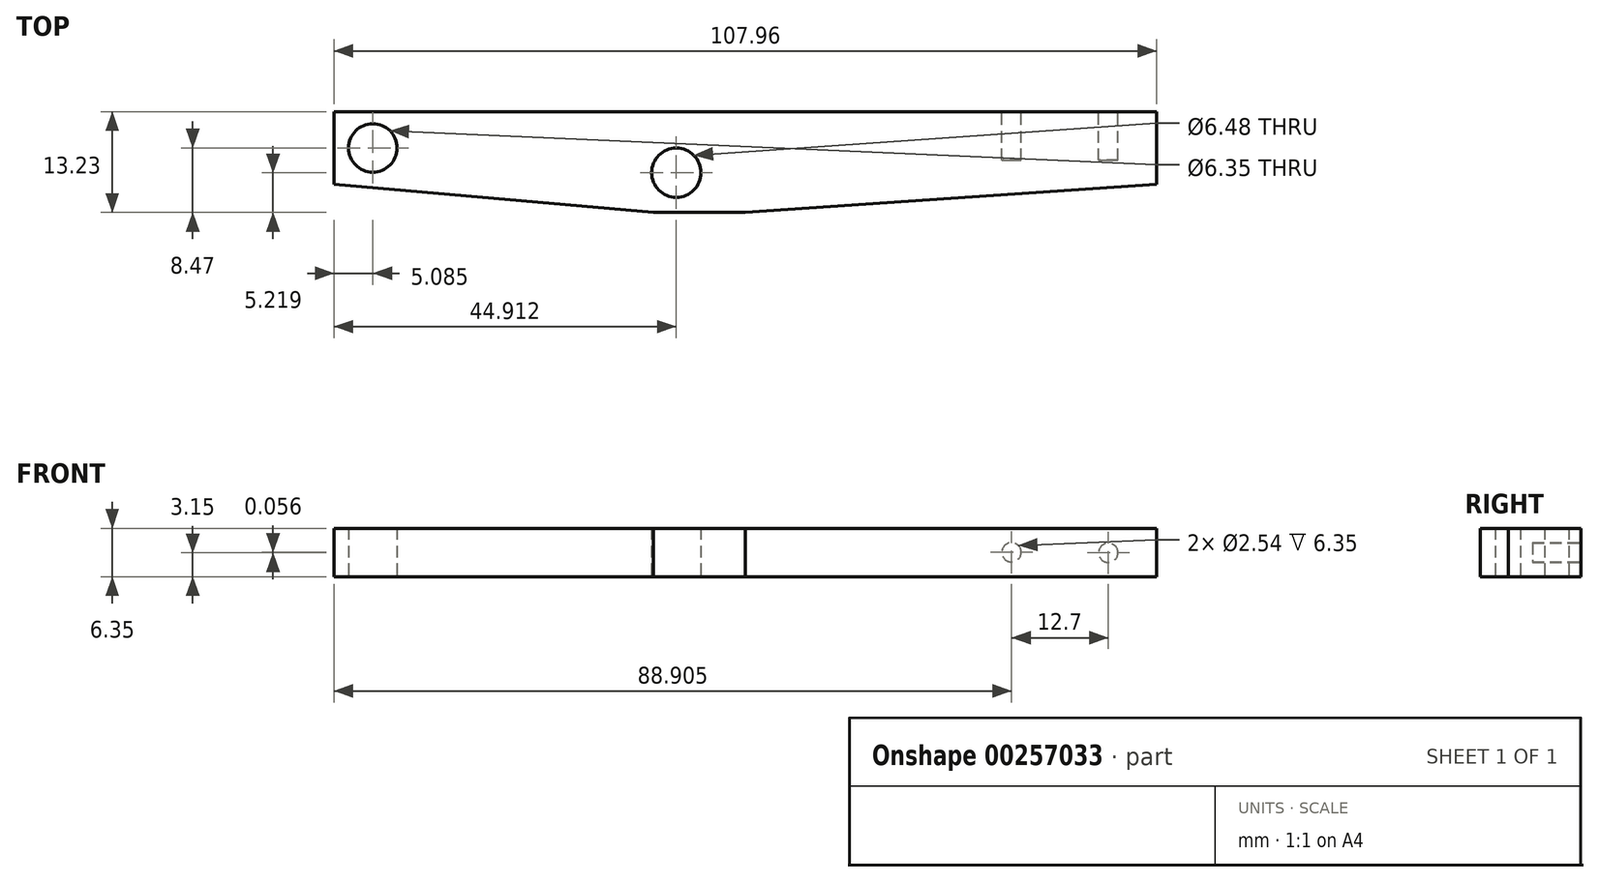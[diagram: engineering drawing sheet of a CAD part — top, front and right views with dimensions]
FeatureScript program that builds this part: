
annotation { "Feature Type Name" : "Feature", "Feature Type Description" : "" }
export const myFeature = defineFeature(function(context is Context, id is Id, definition is map)
    precondition{}
    {
        {
            var Q0;
            Q0=qCreatedBy(makeId("Top.planeOp"),FACE);
            var sketch = newSketch(context, id + "F0", { "sketchPlane" : qUnion([Q0])});
            skLineSegment(sketch, "E0.bottom", {"start": v(53.98, 4.76) * mm, "end": v(-53.98, 4.76) * mm});
            skLineSegment(sketch, "E0.top", {"start": v(53.98, -4.76) * mm, "end": v(-53.98, -4.76) * mm});
            skLineSegment(sketch, "E0.left", {"start": v(53.98, 4.76) * mm, "end": v(53.98, -4.76) * mm});
            skLineSegment(sketch, "E0.right", {"start": v(-53.98, 4.76) * mm, "end": v(-53.98, -4.76) * mm});
            skPoint(sketch, "E0.middle", {"position": v(0, 0) * mm});
            skLineSegment(sketch, "E1", {"start": v(-53.98, -4.76) * mm, "end": v(-12.07, -8.47) * mm});
            skLineSegment(sketch, "E2", {"start": v(-12.06, -8.47) * mm, "end": v(0, -8.47) * mm});
            skLineSegment(sketch, "E3", {"start": v(0, -8.47) * mm, "end": v(53.98, -4.76) * mm});
            skCircle(sketch, "E4", {"center": v(-48.9, 0) * mm, "radius": 3.18 * mm});
            skCircle(sketch, "E5", {"center": v(-9.07, -3.25) * mm, "radius": 3.24 * mm});
            skSolve(sketch);
        }
        {
            var Q0;
            Q0 = qSketchRegion(id + "F0", true);
            extrude(context, id + "F1", {"entities" : qUnion([Q0]), "depth" : 6.35 * mm});
        }
        {
            var Q0;
            Q0=makeQuery(id+"F1.opExtrude","SWEPT_FACE",FACE,{"disambiguationData":[OSD([sQuery(id+"F0.wireOp",EDGE,"E0.bottom")])]});
            var sketch = newSketch(context, id + "F2", { "sketchPlane" : qUnion([Q0])});
            skCircle(sketch, "E6", {"center": v(-47.62, 3.15) * mm, "radius": 1.27 * mm});
            skCircle(sketch, "E7", {"center": v(-34.92, 3.2) * mm, "radius": 1.27 * mm});
            skSolve(sketch);
        }
        {
            var Q0;
            Q0 = qSketchRegion(id + "F2", true);
            extrude(context, id + "F3", {"entities" : qUnion([Q0]), "operationType" : NewBodyOperationType.REMOVE, "oppositeDirection" : true, "depth" : 6.35 * mm});
        }
    });
